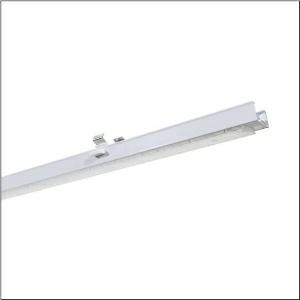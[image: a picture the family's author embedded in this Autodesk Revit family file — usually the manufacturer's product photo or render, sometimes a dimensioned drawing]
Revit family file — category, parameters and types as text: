
# Revit family: sanierungs-leuchteneinsatz_31_gen_2_51re19mb4cb_bacd
name_source: partatom
category: Lighting Fixtures
units: mm (PartAtom-declared; Revit-internal decimal feet)

## family parameters
Cut with Voids When Loaded = No
Host = Face
Light Source = No
Part Type = Normal
Room Calculation Point = No
Round Connector Dimension = Use Diameter
Shared = No

## types (1)
- --- (1 x LED, 11500 lm, 66 W, 4000K)
    Apparent Load = 66 VA
    CIE Flux Codes = 66 89 98 99 100
    Color Rendering = 80
    Color Temperature = 4000K
    Default Elevation = 1800 mm
    Description = Refurbishment luminaire insert Gen.2, luminaire insert, of extruded aluminium section, coated, traffic white (RAL 9016), length: 1.472mm, width: 91mm, height: 53mm, LED rated luminous flux: 11.500lm, light colour: 840, control gear: ON/OFF Multilumen, control gear: ECG Multilumen, with system connector: socket, mains connection: 220..240V, AC, 50/60Hz, connected load according to luminous flux setting (19/24/32/37/47/52/60/66W), luminous flux adjustable on luminaire in eight steps (3450/4380/5800/6700/8350/9200/10500/11500lm ), primary light control with lens, of plastic, primary optical cover: cover, of PMMA, light emission: direct distribution, primary light characteristic: double asymmetric, protection rating (complete): IP20, insulation class (complete): insulation class I (protective earthing), certification: CE, UKCA, permissible ambient temperature for indoor applications: -20..+40°C, packaging unit: 1 piece
    Height = 58 mm
    Lamp = 1 x LED
    Lamp Light Flux = 11500 lm
    Lamp Power = 66 W
    Lamp count = 1
    Length = 1472 mm
    Luminous efficacy = 174 lm/W
    Manufacturer = Siteco
    ModVariant = No
    Model = 51RE19MB4CB
    Mounting Place = Ceiling
    Mounting Type = Pendant
    Number of Poles = 1
    OnlyDefault = Yes
    Power Factor = 1
    Product Name = Sanierungs-Leuchteneinsatz 31 Gen.2
    Product group = luminaire insert
    ProductGroupID = 902
    Protection Class = Protection class I
    Protection Degree = IP 20
    RLX_Detail_Level = 1
    RlxData = <blob elided: 21201 chars, md5=689a8506>
    Socket = socket
    Standby Power = 0 W
    System Light Flux = 11500 lm
    System Power = 66 W
    Type Comments = factory setting: luminous flux: 100 % | (ON | ON | ON)
    Type Image = l_1266702.jpg
    URL = http://relux.com
    VarID = @adj_067993
    Voltage = 0 V
    Weight = 0.00 kg
    Width = 65 mm

## geometry (parser evidence)
native form markers: Blend x4, Sweep x9
no freeform markers — native parametric forms only
